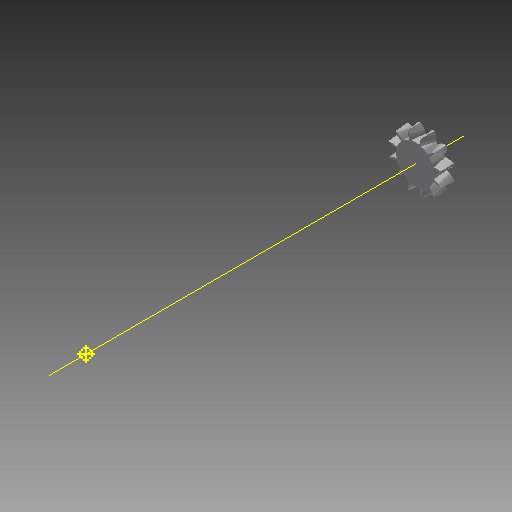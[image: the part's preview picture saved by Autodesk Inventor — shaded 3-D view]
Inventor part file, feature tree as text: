
AUTODESK INVENTOR PART (.ipt)
format: ipt  version: 2017 (Build 210142000, 142)  size: 449,024 bytes
history: native  units: mm
features: other x24, loft x2, pattern_circular x2, sketch x1
ambient origin geometry x6: Origin, XZ Plane, X Axis, Y Axis, Z Axis, Center Point
bodies: Solid1 (feature_tree)
feature tree (29):
  other  "Top Point"
  other  "Mesh Plane2"
  other  "Teeth Body"
  other  "Start Point"
  other  "Tooth Plane"
  other  "Start Sketch"
  other  "End Point"
  other  "3D Sketch Right"
  other  "End Plane Right"
  loft  "Loft Right"
  pattern_circular  "Circular Pattern Right"  [2 undecoded]
  other  "3D Sketch Left"
  other  "End Plane Left"
  loft  "Loft Left"
  pattern_circular  "Circular Pattern Left"  [2 undecoded]
  other  "Fix Body"
  other  "Mesh Plane"
  other  "Top Plane"
  other  "Teeth Body Sketch"
  other  "End Plane"
  other  "End Sketch"
  other  "Helical Curve Left"
  other  "End Sketch Left"
  other  "Body Sketch"
  sketch  "Sketch6"  dims[d0=20.32mm d1=16.688265mm d2=23.784811mm d3=5.08mm d4=144.658428mm d5=90.0deg d7=5.001948mm d8=5.466843mm d9=7.461787mm d11=5.25785mm d17=0.0mm d18=90.0deg d19=0.0mm d20=90.0deg d21=120.0mm d22=360.0deg d26=126.354885mm d27=5.244951mm d28=20.32mm d29=-0.700606mm d30=4.825744mm d31=5.274263mm d32=7.19893mm d35=0.0mm d37=0.0mm d39=0.0mm d40=90.0deg d41=120.0mm d42=360.0deg d46=90.0deg d47=90.0deg d48=0.0mm d49=0.0mm d50=90.0deg d51=15.0deg d52=0.0mm d53=0.0mm d54=0.0mm d56=11.448008mm d57=12.988752mm d58=7.937813mm d59=12.531197mm d60=7.658187mm d61=12.531197mm d62=7.658187mm d63=90.0deg d64=90.0deg d65=126.354885mm d66=31.5mm d67=20.32mm d68=-0.700606mm d69=5.244951mm d70=5.274263mm d71=7.19893mm d72=4.825744mm d73=7.658187mm d74=12.531197mm d75=0.0mm d76=90.0deg d77=0.0mm d78=90.0deg d79=0.0mm d80=90.0deg d81=120.0mm d82=360.0deg d84=10.0mm d85=20.0mm d86=20.0mm d87=10.0mm d88=0.0mm d89=0.0mm d90=0.635mm]
  other  "Srf1"
  other  "Helical Curve Right"
  other  "End Sketch Right"
  other  "Pitch Diameter"
note: 4 required parameter values undecoded (feature->parameter linkage not recoverable at this tier; creation-order binding heuristic only, values carry confidence <= 0.55)
